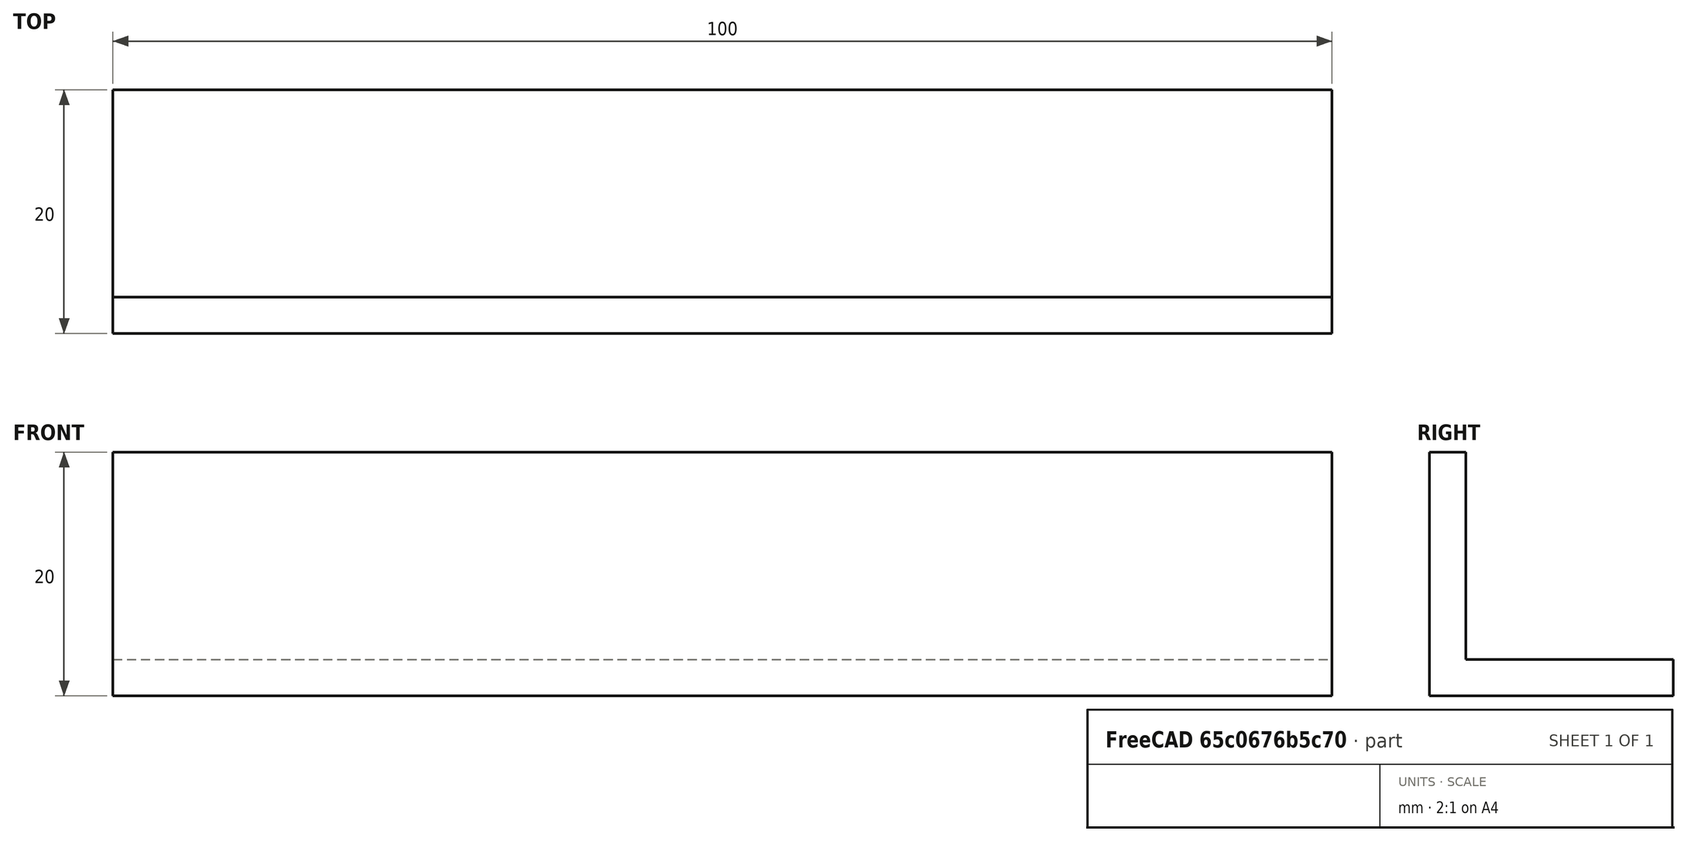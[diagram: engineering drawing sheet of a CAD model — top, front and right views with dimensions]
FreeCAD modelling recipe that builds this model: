
FCSTD DOCUMENT  (FreeCAD 1.0R39109 (Git))
Label: angulo_20x20
License: All rights reserved
LicenseURL: https://en.wikipedia.org/wiki/All_rights_reserved
objects: Sketcher::SketchObject×1, PartDesign::Pad×1, PartDesign::Body×1
note: 6 computed .brp shape members not serialized (recipe doc carries the construction recipe); baked Part::Feature solids carry a one-line shape summary decoded from their .brp

FEATURE [Sketcher::SketchObject] Sketch
  ArcFitTolerance = 1e-06
  AttachmentSupport = -> [YZ_Plane]
  FullyConstrained = true
  MakeInternals = false
  MapMode = 5
  Placement = pos=(0,0,0) rot=(0.57735,0.57735,0.57735;2.0944rad)
  sketch-geometry (6):
    g0: LineSegment StartX=0 StartY=0 StartZ=0 EndX=20 EndY=0 EndZ=0
    g1: LineSegment StartX=20 StartY=3 StartZ=0 EndX=3 EndY=3 EndZ=0
    g2: LineSegment StartX=3 StartY=20 StartZ=0 EndX=-2.012e-13 EndY=20 EndZ=0
    g3: LineSegment StartX=0 StartY=0 StartZ=0 EndX=-2.013e-13 EndY=20 EndZ=0
    g4: LineSegment StartX=3 StartY=20 StartZ=0 EndX=3 EndY=3 EndZ=0
    g5: LineSegment StartX=20 StartY=0 StartZ=0 EndX=20 EndY=3 EndZ=0
  constraints (17):
    c: Coincident(g0,g-1)
    c: PointOnObject(g0,g-1)
    c: Horizontal(g1)
    c: Horizontal(g2)
    c: Coincident(g3,g0)
    c: Coincident(g3,g2)
    c: Coincident(g4,g2)
    c: Coincident(g4,g1)
    c: Vertical(g4)
    c: Coincident(g5,g0)
    c: Coincident(g5,g1)
    c: Parallel(g4,g3)
    c: Parallel(g5,g3)
    c: DistanceX(g0,g0) = 20
    c: Equal(g3,g0)
    c: Equal(g1,g4)
    c: DistanceY(g5,g5) = 3
FEATURE [PartDesign::Pad] Pad
  Direction = (1,0,0)
  Length = 100
  Length2 = 10
  Placement = pos=(0,0,0) rot=(1,1,1;2.0944rad)
  Profile = -> Sketch
  ReferenceAxis = -> Sketch [N_Axis]
  Refine = true
  Suppressed = false
  Type = 0
FEATURE [PartDesign::Body] Body  label="Cuerpo"
  AllowCompound = false
  Group = -> [Sketch,Pad]
  Origin = -> Origin
  Tip = -> Pad
